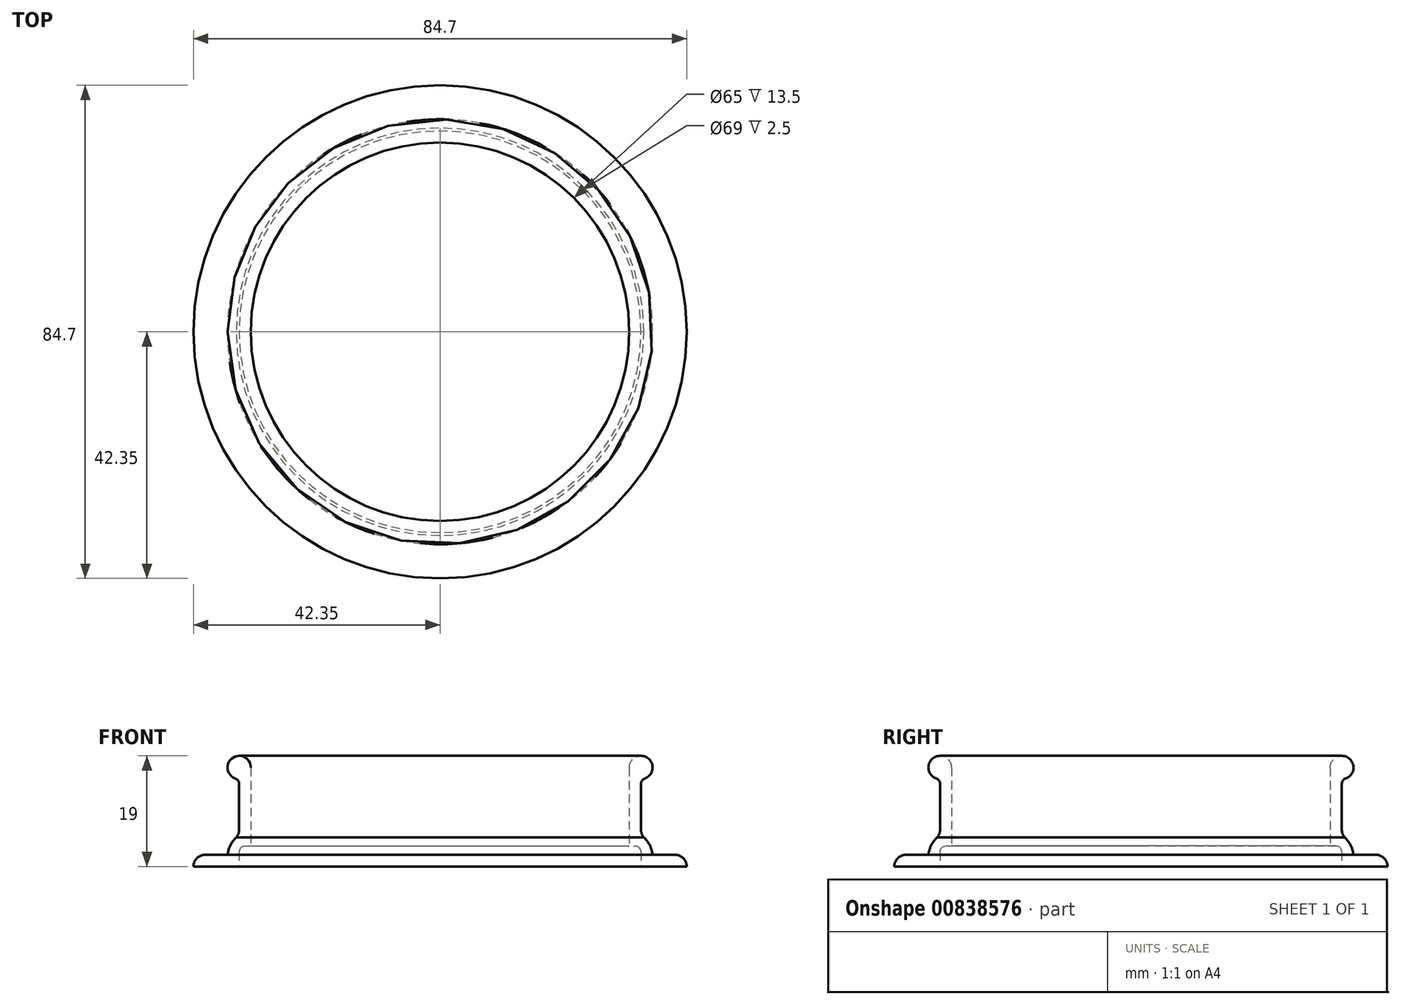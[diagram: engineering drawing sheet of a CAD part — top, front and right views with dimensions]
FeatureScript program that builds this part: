
annotation { "Feature Type Name" : "Feature", "Feature Type Description" : "" }
export const myFeature = defineFeature(function(context is Context, id is Id, definition is map)
    precondition{}
    {
        {
            var Q0;
            Q0=qCreatedBy(makeId("Top.planeOp"),FACE);
            var sketch = newSketch(context, id + "F0", { "sketchPlane" : qUnion([Q0])});
            skCircle(sketch, "E0", {"center": v(0, 0) * mm, "radius": 42 * mm});
            skCircle(sketch, "E1", {"center": v(0, 0) * mm, "radius": 36.5 * mm});
            skSolve(sketch);
        }
        {
            var Q0;
            Q0=qSketchRegion(id+"F0",true);
            extrude(context, id + "F1", {"entities" : qUnion([Q0]), "depth" : 2 * mm, "offsetDistance" : 25 * mm});
        }
        {
            var Q0;
            Q0=qCreatedBy(makeId("Front.planeOp"),FACE);
            var sketch = newSketch(context, id + "F2", { "sketchPlane" : qUnion([Q0])});
            skLineSegment(sketch, "E2", {"start": v(0, 0) * mm, "end": v(0, 127.1) * mm, "construction": true});
            skLineSegment(sketch, "E3.0", {"start": v(-36.5, 0) * mm, "end": v(0, 0) * mm});
            skLineSegment(sketch, "E4.0", {"start": v(-36.5, 2) * mm, "end": v(0, 2) * mm});
            skLineSegment(sketch, "E5", {"start": v(36.5, 2) * mm, "end": v(36.5, 0) * mm});
            skLineSegment(sketch, "E6", {"start": v(34.5, 3) * mm, "end": v(34.5, 14.17) * mm});
            skLineSegment(sketch, "E7", {"start": v(32.5, 2) * mm, "end": v(32.5, 17) * mm});
            skLineSegment(sketch, "E8.trimOffspring", {"start": v(35.5, 2) * mm, "end": v(36.5, 2) * mm});
            skLineSegment(sketch, "E9.trimOffspring", {"start": v(34.5, 0) * mm, "end": v(36.5, 0) * mm});
            skArc(sketch, "E10", {"start": v(35.17, 15.11) * mm, "mid": v(35.65, 18.63) * mm, "end": v(32.5, 17) * mm});
            skPoint(sketch, "E11.visualSharp", {"position": v(34.5, 2) * mm});
            skArc(sketch, "E11.filletArc", {"start": v(34.5, 3) * mm, "mid": v(34.8, 2.3) * mm, "end": v(35.5, 2) * mm});
            skPoint(sketch, "E12.visualSharp", {"position": v(32.5, 0) * mm});
            skArc(sketch, "E12.filletArc", {"start": v(32.5, 2) * mm, "mid": v(33.09, 0.59) * mm, "end": v(34.5, 0) * mm});
            skPoint(sketch, "E13.visualSharp", {"position": v(34.5, 15) * mm});
            skArc(sketch, "E13.filletArc", {"start": v(35.17, 15.11) * mm, "mid": v(34.68, 14.75) * mm, "end": v(34.5, 14.17) * mm});
            skSolve(sketch);
        }
        {
            var Q0;
            Q0=qSketchRegion(id+"F2",true);
            var Q1;
            Q1=sQuery(id+"F2.wireOp",EDGE,"E2");
            revolve(context, id + "F3", {"operationType" : NewBodyOperationType.ADD, "surfaceOperationType" : NewSurfaceOperationType.NEW, "entities" : qUnion([Q0]), "axis" : qUnion([Q1]), "revolveType" : RevolveType.FULL});
        }
        {
            var Q0;
            Q0=makeQuery(id+"F3.boolean.opBoolean","MERGE",FACE,{"derivedFrom":[makeQuery(id+"F1.opExtrude","CAP_FACE",FACE,{"disambiguationData":[OSD([sQuery(id+"F0.wireOp",EDGE,"E0"),sQuery(id+"F0.wireOp",EDGE,"E1")])],"isStart":true}),makeQuery(id+"F3.opRevolve","SWEPT_FACE",FACE,{"disambiguationData":[OSD([sQuery(id+"F2.wireOp",EDGE,"E9.trimOffspring")])]})]});
            var sketch = newSketch(context, id + "F4", { "sketchPlane" : qUnion([Q0])});
            skCircle(sketch, "E14.0", {"center": v(0, 0) * mm, "radius": 42 * mm});
            skSolve(sketch);
        }
        {
            var Q0;
            Q0=qSketchRegion(id+"F4",true);
            extrude(context, id + "F5", {"entities" : qUnion([Q0]), "operationType" : NewBodyOperationType.ADD, "oppositeDirection" : true, "depth" : 1 * mm, "offsetDistance" : 25 * mm});
        }
        {
            var Q0;
            Q0=makeQuery(id+"F5.opExtrude","CAP_FACE",FACE,{"disambiguationData":[OSD([sQuery(id+"F4.wireOp",EDGE,"E14.0")])],"isStart":false});
            var sketch = newSketch(context, id + "F6", { "sketchPlane" : qUnion([Q0])});
            skCircle(sketch, "E15.0", {"center": v(0, 0) * mm, "radius": 34.5 * mm});
            skCircle(sketch, "E16.0", {"center": v(0, 0) * mm, "radius": 32.5 * mm});
            skSolve(sketch);
        }
        {
            var Q0;
            Q0=qSketchRegion(id+"F6",true);
            extrude(context, id + "F7", {"entities" : qUnion([Q0]), "operationType" : NewBodyOperationType.ADD, "depth" : 3 * mm, "offsetDistance" : 25 * mm});
        }
        {
            var Q0;
            Q0=makeQuery(id+"F3.boolean.opBoolean","MERGE",FACE,{"derivedFrom":[makeQuery(id+"F1.opExtrude","CAP_FACE",FACE,{"disambiguationData":[OSD([sQuery(id+"F0.wireOp",EDGE,"E0"),sQuery(id+"F0.wireOp",EDGE,"E1")])],"isStart":false}),makeQuery(id+"F3.opRevolve","SWEPT_FACE",FACE,{"disambiguationData":[OSD([sQuery(id+"F2.wireOp",EDGE,"E8.trimOffspring")])]})]});
            var sketch = newSketch(context, id + "F8", { "sketchPlane" : qUnion([Q0])});
            skCircle(sketch, "E17.0", {"center": v(0, 0) * mm, "radius": 42 * mm});
            skCircle(sketch, "E18", {"center": v(0, 0) * mm, "radius": 42.35 * mm});
            skSolve(sketch);
        }
        {
            var Q0;
            Q0=qSketchRegion(id+"F8",true);
            extrude(context, id + "F9", {"entities" : qUnion([Q0]), "operationType" : NewBodyOperationType.ADD, "oppositeDirection" : true, "depth" : 2 * mm, "offsetDistance" : 25 * mm});
        }
        {
            var Q0;
            Q0=makeQuery(id+"F9.opExtrude","CAP_EDGE",EDGE,{"disambiguationData":[OSD([sQuery(id+"F8.wireOp",EDGE,"E18")])],"isStart":true});
            fillet(context, id + "F10", {"entities" : qUnion([Q0]), "radius" : 2 * mm, "tangentPropagation" : true, "allowEdgeOverflow" : false});
        }
        {
            var Q0;
            Q0=makeQuery(id+"F9.boolean.opBoolean","MERGE",FACE,{"derivedFrom":[makeQuery(id+"F5.boolean.opBoolean","MERGE",FACE,{"derivedFrom":[makeQuery(id+"F3.boolean.opBoolean","MERGE",FACE,{"derivedFrom":[makeQuery(id+"F1.opExtrude","CAP_FACE",FACE,{"disambiguationData":[OSD([sQuery(id+"F0.wireOp",EDGE,"E0"),sQuery(id+"F0.wireOp",EDGE,"E1")])],"isStart":true}),makeQuery(id+"F3.opRevolve","SWEPT_FACE",FACE,{"disambiguationData":[OSD([sQuery(id+"F2.wireOp",EDGE,"E9.trimOffspring")])]})]}),makeQuery(id+"F5.opExtrude","CAP_FACE",FACE,{"disambiguationData":[OSD([sQuery(id+"F4.wireOp",EDGE,"E14.0")])],"isStart":true})]}),makeQuery(id+"F9.opExtrude","CAP_FACE",FACE,{"disambiguationData":[OSD([sQuery(id+"F8.wireOp",EDGE,"E17.0"),sQuery(id+"F8.wireOp",EDGE,"E18")])],"isStart":false})]});
            var sketch = newSketch(context, id + "F11", { "sketchPlane" : qUnion([Q0])});
            skCircle(sketch, "E19.0", {"center": v(0, 0) * mm, "radius": 32.5 * mm});
            skSolve(sketch);
        }
        {
            var Q0;
            Q0 = qSketchRegion(id + "F11", true);
            extrude(context, id + "F12", {"entities" : qUnion([Q0]), "operationType" : NewBodyOperationType.REMOVE, "oppositeDirection" : true, "depth" : 25 * mm, "offsetDistance" : 25 * mm});
        }
        {
            var Q0;
            Q0=makeQuery(id+"F9.boolean.opBoolean","MERGE",FACE,{"derivedFrom":[makeQuery(id+"F5.boolean.opBoolean","MERGE",FACE,{"derivedFrom":[makeQuery(id+"F3.boolean.opBoolean","MERGE",FACE,{"derivedFrom":[makeQuery(id+"F1.opExtrude","CAP_FACE",FACE,{"disambiguationData":[OSD([sQuery(id+"F0.wireOp",EDGE,"E0"),sQuery(id+"F0.wireOp",EDGE,"E1")])],"isStart":true}),makeQuery(id+"F3.opRevolve","SWEPT_FACE",FACE,{"disambiguationData":[OSD([sQuery(id+"F2.wireOp",EDGE,"E9.trimOffspring")])]})]}),makeQuery(id+"F5.opExtrude","CAP_FACE",FACE,{"disambiguationData":[OSD([sQuery(id+"F4.wireOp",EDGE,"E14.0")])],"isStart":true})]}),makeQuery(id+"F9.opExtrude","CAP_FACE",FACE,{"disambiguationData":[OSD([sQuery(id+"F8.wireOp",EDGE,"E17.0"),sQuery(id+"F8.wireOp",EDGE,"E18")])],"isStart":false})]});
            var sketch = newSketch(context, id + "F13", { "sketchPlane" : qUnion([Q0])});
            skCircle(sketch, "E20.0", {"center": v(0, 0) * mm, "radius": 32.5 * mm});
            skCircle(sketch, "E21", {"center": v(0, 0) * mm, "radius": 36.5 * mm});
            skSolve(sketch);
        }
        {
            var Q0;
            Q0 = qSketchRegion(id + "F13", true);
            extrude(context, id + "F14", {"entities" : qUnion([Q0]), "operationType" : NewBodyOperationType.ADD, "oppositeDirection" : true, "depth" : 5 * mm, "offsetDistance" : 25 * mm});
        }
        {
            var Q0;
            Q0=makeQuery(id+"F9.boolean.opBoolean","MERGE",FACE,{"derivedFrom":[makeQuery(id+"F5.boolean.opBoolean","MERGE",FACE,{"derivedFrom":[makeQuery(id+"F3.boolean.opBoolean","MERGE",FACE,{"derivedFrom":[makeQuery(id+"F1.opExtrude","CAP_FACE",FACE,{"disambiguationData":[OSD([sQuery(id+"F0.wireOp",EDGE,"E0"),sQuery(id+"F0.wireOp",EDGE,"E1")])],"isStart":true}),makeQuery(id+"F3.opRevolve","SWEPT_FACE",FACE,{"disambiguationData":[OSD([sQuery(id+"F2.wireOp",EDGE,"E9.trimOffspring")])]})]}),makeQuery(id+"F5.opExtrude","CAP_FACE",FACE,{"disambiguationData":[OSD([sQuery(id+"F4.wireOp",EDGE,"E14.0")])],"isStart":true})]}),makeQuery(id+"F9.opExtrude","CAP_FACE",FACE,{"disambiguationData":[OSD([sQuery(id+"F8.wireOp",EDGE,"E17.0"),sQuery(id+"F8.wireOp",EDGE,"E18")])],"isStart":false})]});
            var sketch = newSketch(context, id + "F15", { "sketchPlane" : qUnion([Q0])});
            skCircle(sketch, "E22", {"center": v(0, 0) * mm, "radius": 34.5 * mm});
            skSolve(sketch);
        }
        {
            var Q0;
            Q0 = qSketchRegion(id + "F15", true);
            extrude(context, id + "F16", {"entities" : qUnion([Q0]), "operationType" : NewBodyOperationType.REMOVE, "oppositeDirection" : true, "depth" : 3.5 * mm, "offsetDistance" : 25 * mm});
        }
        {
            var Q0;
            Q0=makeQuery(id+"F16.boolean.opBoolean","COPY",EDGE,{"derivedFrom":makeQuery(id+"F16.opExtrude","CAP_EDGE",EDGE,{"disambiguationData":[OSD([sQuery(id+"F15.wireOp",EDGE,"E22")])],"isStart":false})});
            fillet(context, id + "F17", {"entities" : qUnion([Q0]), "radius" : 1 * mm, "tangentPropagation" : true, "allowEdgeOverflow" : false});
        }
        {
            var Q0;
            Q0=makeQuery(id+"F14.opExtrude","CAP_EDGE",EDGE,{"disambiguationData":[OSD([sQuery(id+"F13.wireOp",EDGE,"E21")])],"isStart":false});
            chamfer(context, id + "F18", {"entities" : qUnion([Q0]), "width" : 1.5 * mm, "tangentPropagation" : true});
        }
        {
            var Q0;
            Q0=makeQuery(id+"F14.boolean.opBoolean","INTERSECT",EDGE,{"derivedFrom":[makeQuery(id+"F3.opRevolve","SWEPT_FACE",FACE,{"disambiguationData":[OSD([sQuery(id+"F2.wireOp",EDGE,"E6")])]}),makeQuery(id+"F14.opExtrude","CAP_FACE",FACE,{"disambiguationData":[OSD([sQuery(id+"F13.wireOp",EDGE,"E20.0"),sQuery(id+"F13.wireOp",EDGE,"E21")])],"isStart":false})]});
            fillet(context, id + "F19", {"entities" : qUnion([Q0]), "radius" : 2 * mm, "tangentPropagation" : true, "allowEdgeOverflow" : false});
        }
        {
            var Q0;
            {var subQ0=sQuery(id+"F13.wireOp",EDGE,"E21");Q0=makeQuery(id+"F18.opChamfer","BLEND_EDGE",EDGE,{"blendedFrom":[makeQuery(id+"F14.opExtrude","CAP_EDGE",EDGE,{"disambiguationData":[OSD([subQ0])],"isStart":false}),makeQuery(id+"F14.opExtrude","SWEPT_FACE",FACE,{"disambiguationData":[OSD([subQ0])]})],"blendedInto":[makeQuery(id+"F14.opExtrude","SWEPT_FACE",FACE,{"disambiguationData":[OSD([subQ0])]})]});}
            fillet(context, id + "F20", {"entities" : qUnion([Q0]), "radius" : 5 * mm, "tangentPropagation" : true, "allowEdgeOverflow" : false});
        }
    });
